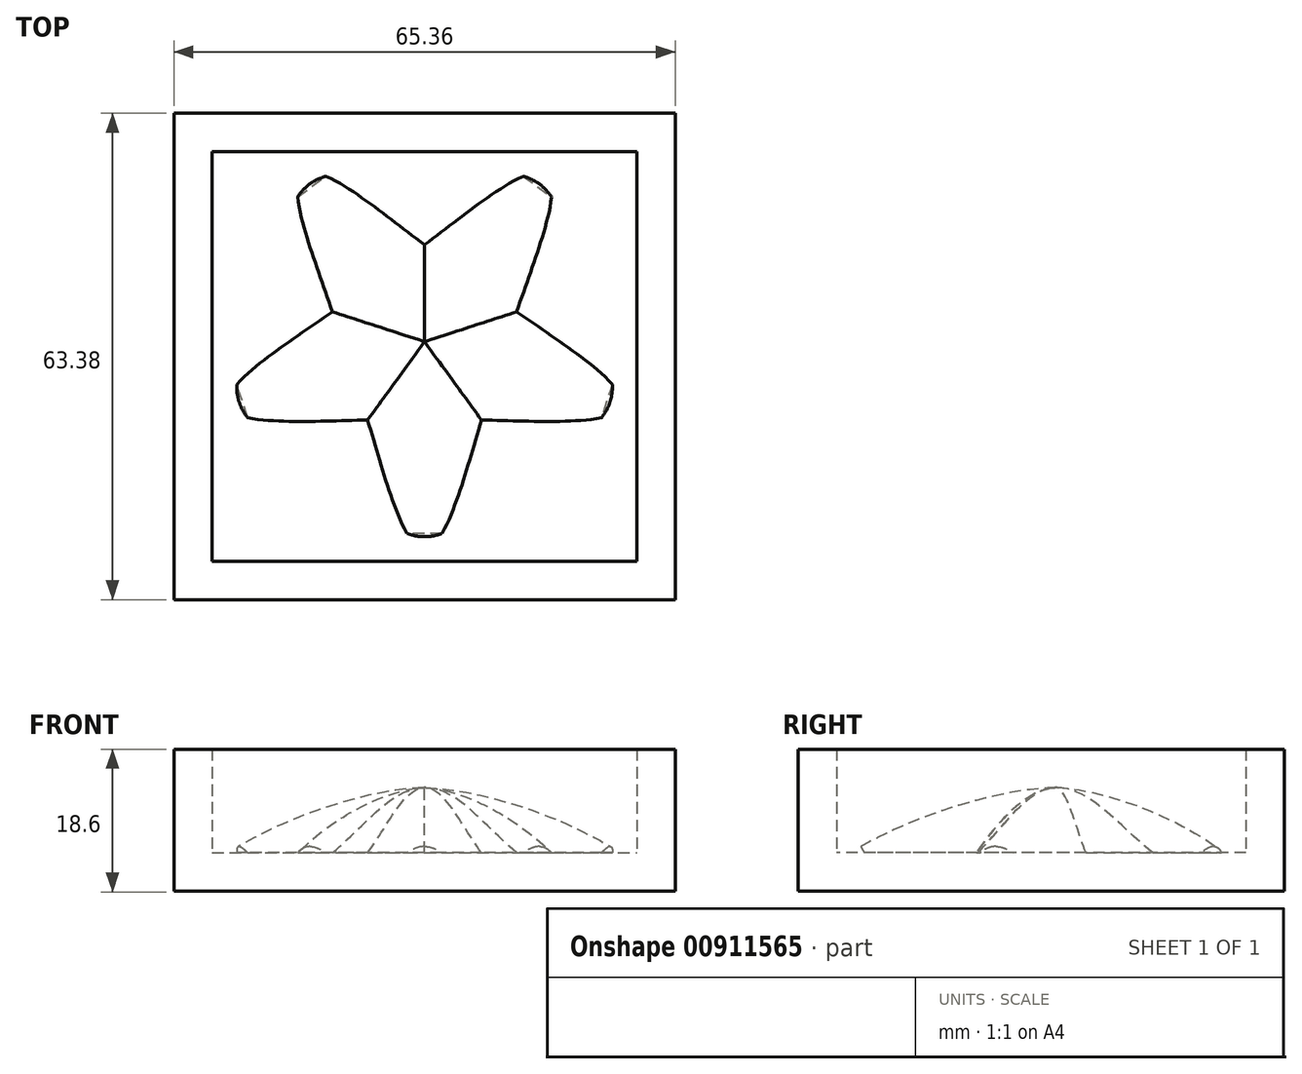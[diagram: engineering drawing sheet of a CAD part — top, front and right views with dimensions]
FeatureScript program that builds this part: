
annotation { "Feature Type Name" : "Feature", "Feature Type Description" : "" }
export const myFeature = defineFeature(function(context is Context, id is Id, definition is map)
    precondition{}
    {
        {
            var Q0;
            Q0=qCreatedBy(makeId("Right.planeOp"),FACE);
            var sketch = newSketch(context, id + "F0", { "sketchPlane" : qUnion([Q0])});
            skFitSpline(sketch, "E0", {"points": [v(0, 7.58) * mm, v(-13, 5.1) * mm, v(-25, 0) * mm], "startDerivative": vector(-24.58, -0.63) * mm, "endDerivative": vector(-25.2, -13.78) * mm});
            skSolve(sketch);
        }
        {
            var Q0;
            Q0=qCreatedBy(makeId("Front.planeOp"),FACE);
            var sketch = newSketch(context, id + "F1", { "sketchPlane" : qUnion([Q0])});
            skFitSpline(sketch, "E1", {"points": [v(0, 8.5) * mm, v(-2.9, 7.02) * mm, v(-6, 3.37) * mm, v(-9.13, 0.73) * mm, v(-14.05, 0) * mm], "startDerivative": vector(-15.17, 0) * mm, "endDerivative": vector(-23.02, 0) * mm});
            skFitSpline(sketch, "E2.MirrorCS", {"points": [v(0, 8.5) * mm, v(2.9, 7.02) * mm, v(6, 3.37) * mm, v(9.13, 0.73) * mm, v(14.05, 0) * mm], "startDerivative": vector(15.17, 0) * mm, "endDerivative": vector(23.02, 0) * mm});
            skLineSegment(sketch, "E3", {"start": v(-14.05, 0) * mm, "end": v(14.05, 0) * mm});
            skSolve(sketch);
        }
        {
            var Q0;
            Q0=makeQuery(id+"F1.imprint","IMPRINT",FACE,{"disambiguationData":[TD([[makeQuery(id+"F1.imprint","IMPRINT",EDGE,{"derivedFrom":sQuery(id+"F1.wireOp",EDGE,"E1")}),1.0]])]});
            var Q1;
            Q1=sQuery(id+"F1.wireOp",EDGE,"E3");
            var Q2;
            Q2=sQuery(id+"F1.wireOp",EDGE,"E2.MirrorCS");
            var Q3;
            Q3=sQuery(id+"F1.wireOp",EDGE,"E1");
            var Q4;
            Q4=sQuery(id+"F0.wireOp",EDGE,"E0");
            sweep(context, id + "F2", {"profiles" : qUnion([Q0]), "surfaceProfiles" : qUnion([Q1, Q2, Q3]), "path" : qUnion([Q4])});
        }
        {
            var Q0;
            Q0=qCreatedBy(makeId("Right.planeOp"),FACE);
            var sketch = newSketch(context, id + "F3", { "sketchPlane" : qUnion([Q0])});
            skLineSegment(sketch, "E4.bottom", {"start": v(0, 0) * mm, "end": v(-102.23, 0) * mm});
            skLineSegment(sketch, "E4.top", {"start": v(0, -29.41) * mm, "end": v(-102.23, -29.41) * mm});
            skLineSegment(sketch, "E4.left", {"start": v(0, 0) * mm, "end": v(0, -29.41) * mm});
            skLineSegment(sketch, "E4.right", {"start": v(-102.23, 0) * mm, "end": v(-102.23, -29.41) * mm});
            skSolve(sketch);
        }
        {
            var Q0;
            Q0=qSketchRegion(id+"F3",true);
            extrude(context, id + "F4", {"entities" : qUnion([Q0]), "operationType" : NewBodyOperationType.REMOVE, "endBound" : BoundingType.THROUGH_ALL, "oppositeDirection" : true, "depth" : 25 * mm, "offsetDistance" : 25 * mm, "hasSecondDirection" : true, "secondDirectionBound" : BoundingType.THROUGH_ALL, "secondDirectionOppositeDirection" : false, "secondDirectionDepth" : 25 * mm});
        }
        {
            var Q0;
            Q0=makeQuery(id+"F2.opSweep","CAP_FACE",FACE,{"disambiguationData":[OSD([sQuery(id+"F1.wireOp",EDGE,"E1"),sQuery(id+"F1.wireOp",EDGE,"E2.MirrorCS"),sQuery(id+"F1.wireOp",EDGE,"E3"),sQuery(id+"F0.wireOp",VERTEX,"E0.start")])],"isStart":true});
            var sketch = newSketch(context, id + "F5", { "sketchPlane" : qUnion([Q0])});
            skLineSegment(sketch, "E5", {"start": v(0, 0) * mm, "end": v(0, 8.5) * mm});
            skSolve(sketch);
        }
        {
            var Q0;
            Q0=makeQuery(id+"F2.opSweep","SWEPT_BODY",BODY,{"disambiguationData":[OSD([sQuery(id+"F1.wireOp",EDGE,"E1"),sQuery(id+"F1.wireOp",EDGE,"E2.MirrorCS"),sQuery(id+"F1.wireOp",EDGE,"E3"),sQuery(id+"F0.wireOp",EDGE,"E0")])]});
            var Q1;
            Q1=sQuery(id+"F5.wireOp",EDGE,"E5");
            circularPattern(context, id + "F6", {"operationType" : NewBodyOperationType.ADD, "entities" : qUnion([Q0]), "axis" : qUnion([Q1]), "angle" : 360 * degree, "instanceCount" : 5, "equalSpace" : true});
        }
        {
            var Q0;
            Q0=makeQuery(id+"F6.opPattern","COPY",FACE,{"derivedFrom":makeQuery(id+"F2.opSweep","CAP_FACE",FACE,{"disambiguationData":[OSD([sQuery(id+"F1.wireOp",EDGE,"E1"),sQuery(id+"F1.wireOp",EDGE,"E2.MirrorCS"),sQuery(id+"F1.wireOp",EDGE,"E3"),sQuery(id+"F0.wireOp",VERTEX,"E0.end")])],"isStart":false}),"instanceName":"3"});
            var sketch = newSketch(context, id + "F7", { "sketchPlane" : qUnion([Q0])});
            skLineSegment(sketch, "E6.0.0", {"start": v(1.44, 11.56) * mm, "end": v(5.76, 10.12) * mm});
            skFitSpline(sketch, "E6.0.1", {"points": [v(17.89, -1.89) * mm, v(15.4, -1.07) * mm, v(12.04, 0.36) * mm, v(9.45, 5.16) * mm, v(7.92, 11.11) * mm, v(5.64, 12.71) * mm, v(4.36, 13.14) * mm]});
            skFitSpline(sketch, "E6.0.2", {"points": [v(4.36, 13.14) * mm, v(3.08, 13.56) * mm, v(0.3, 13.64) * mm, v(-4.5, 9.79) * mm, v(-9.43, 7.49) * mm, v(-12.99, 8.36) * mm, v(-15.47, 9.18) * mm]});
            skSolve(sketch);
        }
        {
            var Q0;
            Q0=qCreatedBy(makeId("Top.planeOp"),FACE);
            var sketch = newSketch(context, id + "F8", { "sketchPlane" : qUnion([Q0])});
            skLineSegment(sketch, "E7.bottom", {"start": v(-27.68, 24.76) * mm, "end": v(27.68, 24.76) * mm});
            skLineSegment(sketch, "E7.top", {"start": v(-27.68, -28.62) * mm, "end": v(27.68, -28.62) * mm});
            skLineSegment(sketch, "E7.left", {"start": v(-27.68, 24.76) * mm, "end": v(-27.68, -28.62) * mm});
            skLineSegment(sketch, "E7.right", {"start": v(27.68, 24.76) * mm, "end": v(27.68, -28.62) * mm});
            skPoint(sketch, "E8.0", {"position": v(-1.22, -25.3) * mm});
            skPoint(sketch, "E9.0", {"position": v(0, -25.42) * mm});
            skLineSegment(sketch, "E10.bottom", {"start": v(-32.68, 29.76) * mm, "end": v(32.68, 29.76) * mm});
            skLineSegment(sketch, "E10.top", {"start": v(-32.68, -33.62) * mm, "end": v(32.68, -33.62) * mm});
            skLineSegment(sketch, "E10.left", {"start": v(-32.68, 29.76) * mm, "end": v(-32.68, -33.62) * mm});
            skLineSegment(sketch, "E10.right", {"start": v(32.68, 29.76) * mm, "end": v(32.68, -33.62) * mm});
            skSolve(sketch);
        }
        {
            var Q0;
            Q0=qSketchRegion(id+"F8",true);
            var Q1;
            Q1=sQuery(id+"F1.wireOp",VERTEX,"E1.start");
            extrude(context, id + "F9", {"entities" : qUnion([Q0]), "endBound" : BoundingType.UP_TO_VERTEX, "depth" : 25 * mm, "endBoundEntityVertex" : qUnion([Q1]), "hasOffset" : true, "offsetDistance" : 5 * mm, "offsetOppositeDirection" : true});
        }
        {
            var Q0;
            Q0=makeQuery(id+"F8.imprint","IMPRINT",FACE,{"disambiguationData":[TD([[makeQuery(id+"F8.imprint","IMPRINT",EDGE,{"derivedFrom":sQuery(id+"F8.wireOp",EDGE,"E7.bottom")}),1.0]])]});
            var Q1;
            Q1=makeQuery(id+"F8.imprint","IMPRINT",FACE,{"disambiguationData":[TD([[makeQuery(id+"F8.imprint","IMPRINT",EDGE,{"derivedFrom":sQuery(id+"F8.wireOp",EDGE,"E7.bottom")}),-1.0]])]});
            extrude(context, id + "F10", {"entities" : qUnion([Q0, Q1]), "operationType" : NewBodyOperationType.ADD, "oppositeDirection" : true, "depth" : 5 * mm, "offsetDistance" : 25 * mm});
        }
    });
